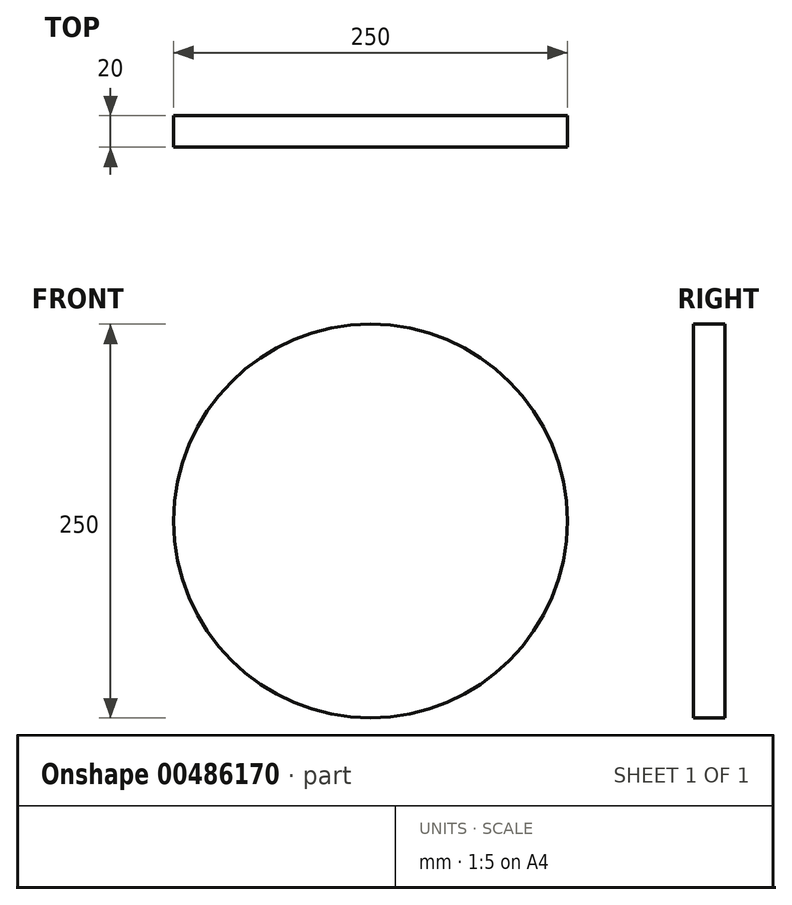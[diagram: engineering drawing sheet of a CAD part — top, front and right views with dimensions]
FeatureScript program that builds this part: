
annotation { "Feature Type Name" : "Feature", "Feature Type Description" : "" }
export const myFeature = defineFeature(function(context is Context, id is Id, definition is map)
    precondition{}
    {
        {
            var Q0;
            Q0=qCreatedBy(makeId("Front.planeOp"),FACE);
            var sketch = newSketch(context, id + "F0", { "sketchPlane" : qUnion([Q0])});
            skCircle(sketch, "E0", {"center": v(0, 0) * mm, "radius": 125 * mm});
            skSolve(sketch);
        }
        {
            var Q0;
            Q0 = qSketchRegion(id + "F0", true);
            extrude(context, id + "F1", {"entities" : qUnion([Q0]), "depth" : 20 * mm});
        }
    });
